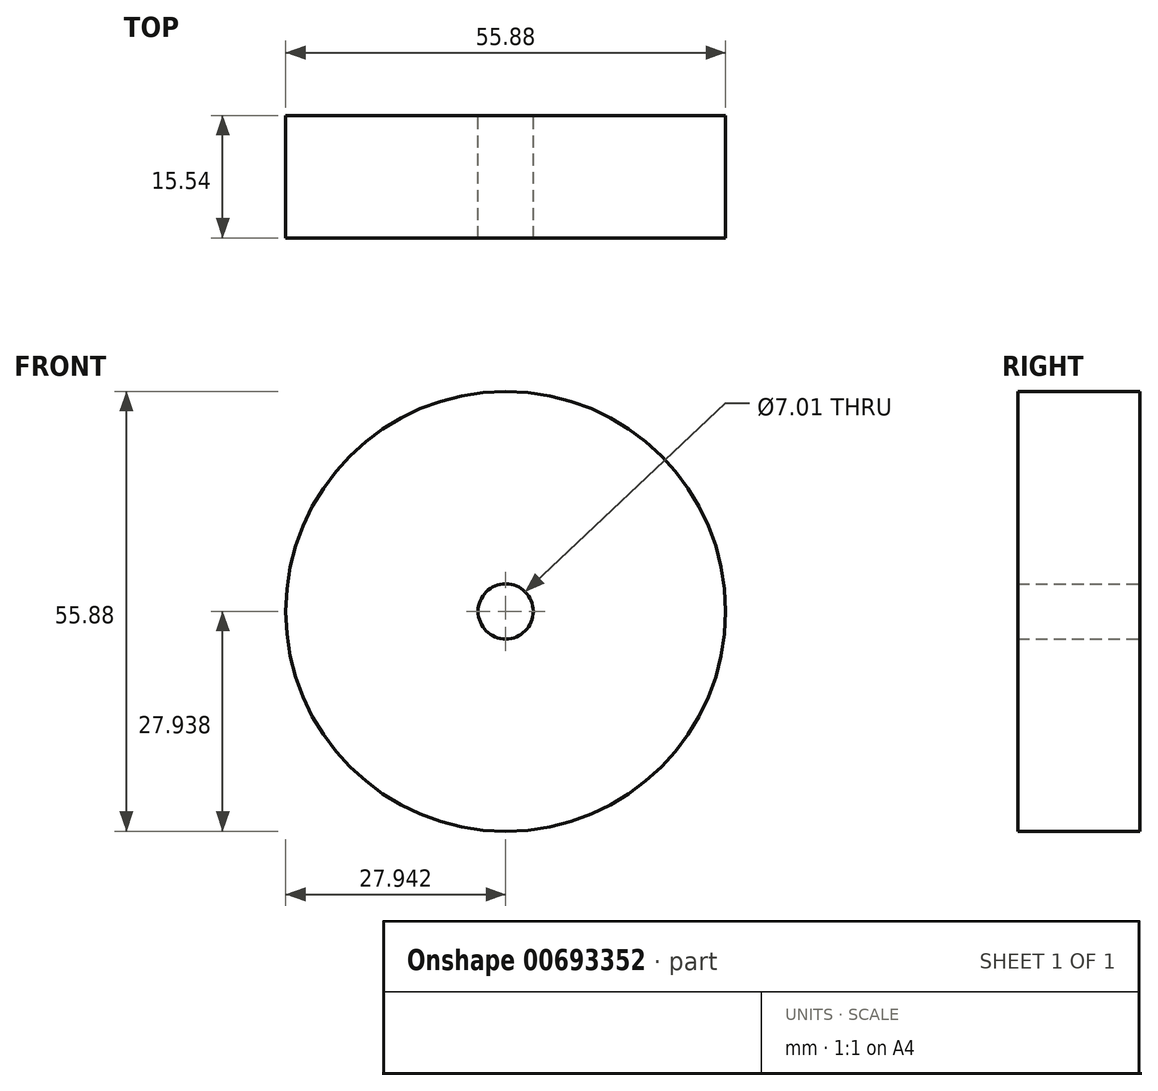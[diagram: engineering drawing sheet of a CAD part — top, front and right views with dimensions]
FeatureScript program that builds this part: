
annotation { "Feature Type Name" : "Feature", "Feature Type Description" : "" }
export const myFeature = defineFeature(function(context is Context, id is Id, definition is map)
    precondition{}
    {
        {
            var Q0;
            Q0=qCreatedBy(makeId("Front.planeOp"),FACE);
            var sketch = newSketch(context, id + "F0", { "sketchPlane" : qUnion([Q0])});
            skCircle(sketch, "E0", {"center": v(-62.16, 39.27) * mm, "radius": 27.94 * mm});
            skCircle(sketch, "E1", {"center": v(-62.16, 39.27) * mm, "radius": 3.5 * mm});
            skSolve(sketch);
        }
        {
            var Q0;
            Q0 = qSketchRegion(id + "F0", true);
            extrude(context, id + "F1", {"entities" : qUnion([Q0]), "endBound" : BoundingType.SYMMETRIC, "depth" : 15.54 * mm, "offsetDistance" : 25.4 * mm});
        }
    });
